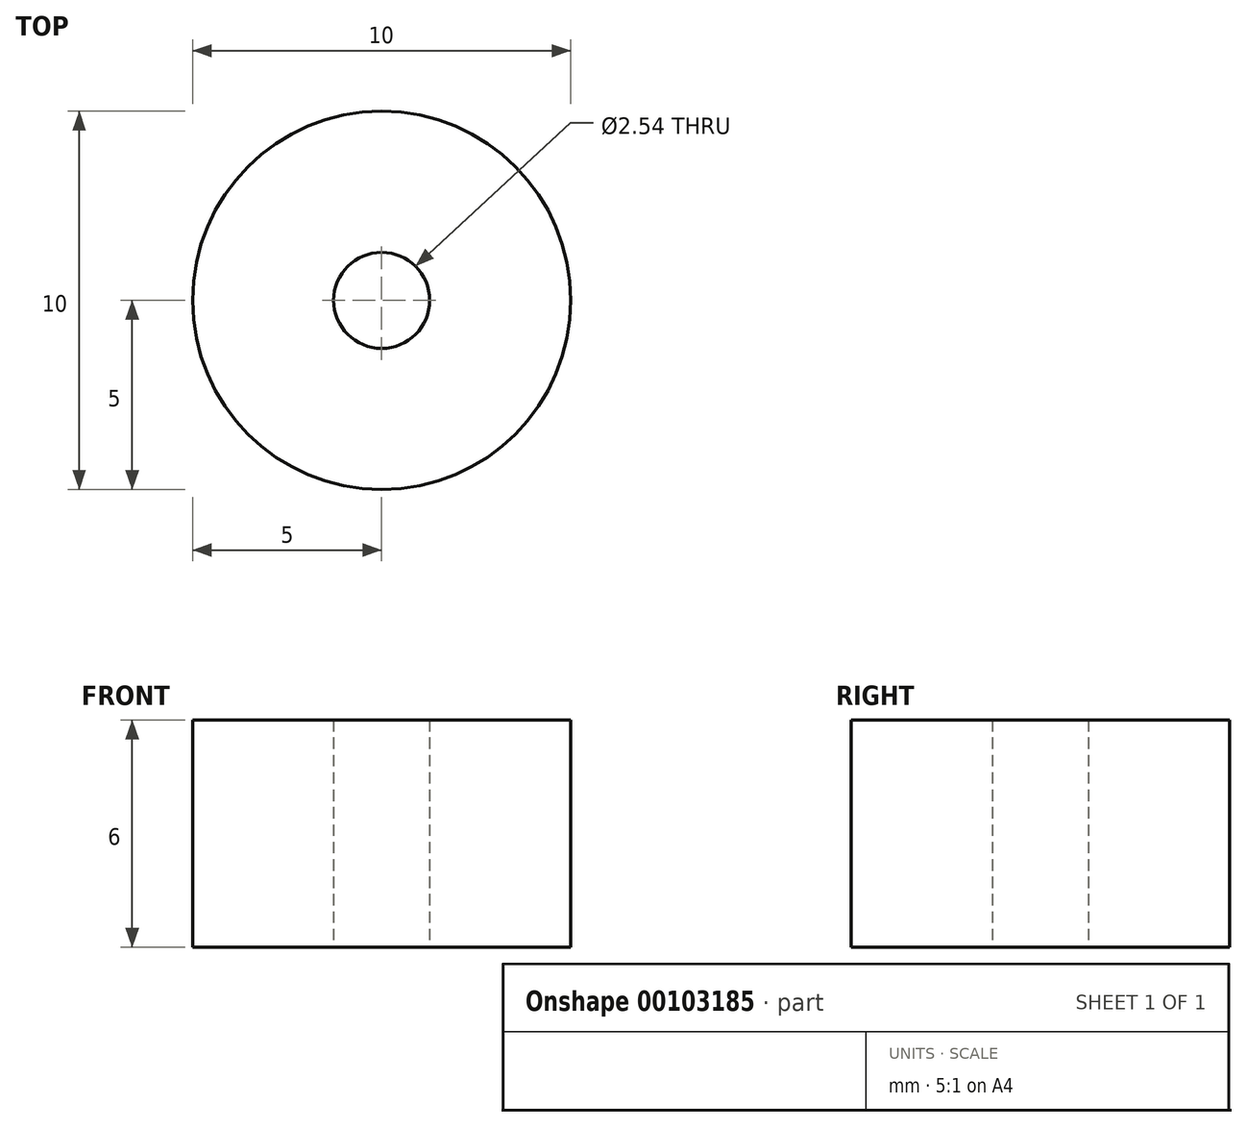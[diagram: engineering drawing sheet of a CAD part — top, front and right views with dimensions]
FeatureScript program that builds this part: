
annotation { "Feature Type Name" : "Feature", "Feature Type Description" : "" }
export const myFeature = defineFeature(function(context is Context, id is Id, definition is map)
    precondition{}
    {
        {
            var Q0;
            Q0=qCreatedBy(makeId("Top.planeOp"),FACE);
            var sketch = newSketch(context, id + "F0", { "sketchPlane" : qUnion([Q0])});
            skCircle(sketch, "E0", {"center": v(0, 0) * mm, "radius": 5 * mm});
            skCircle(sketch, "E1", {"center": v(0, 0) * mm, "radius": 1.27 * mm});
            skSolve(sketch);
        }
        {
            var Q0;
            Q0=makeQuery(id+"F0.imprint","IMPRINT",FACE,{"disambiguationData":[TD([[makeQuery(id+"F0.imprint","IMPRINT",EDGE,{"derivedFrom":sQuery(id+"F0.wireOp",EDGE,"E0")}),1.0]])]});
            extrude(context, id + "F1", {"entities" : qUnion([Q0]), "depth" : 6 * mm});
        }
    });
